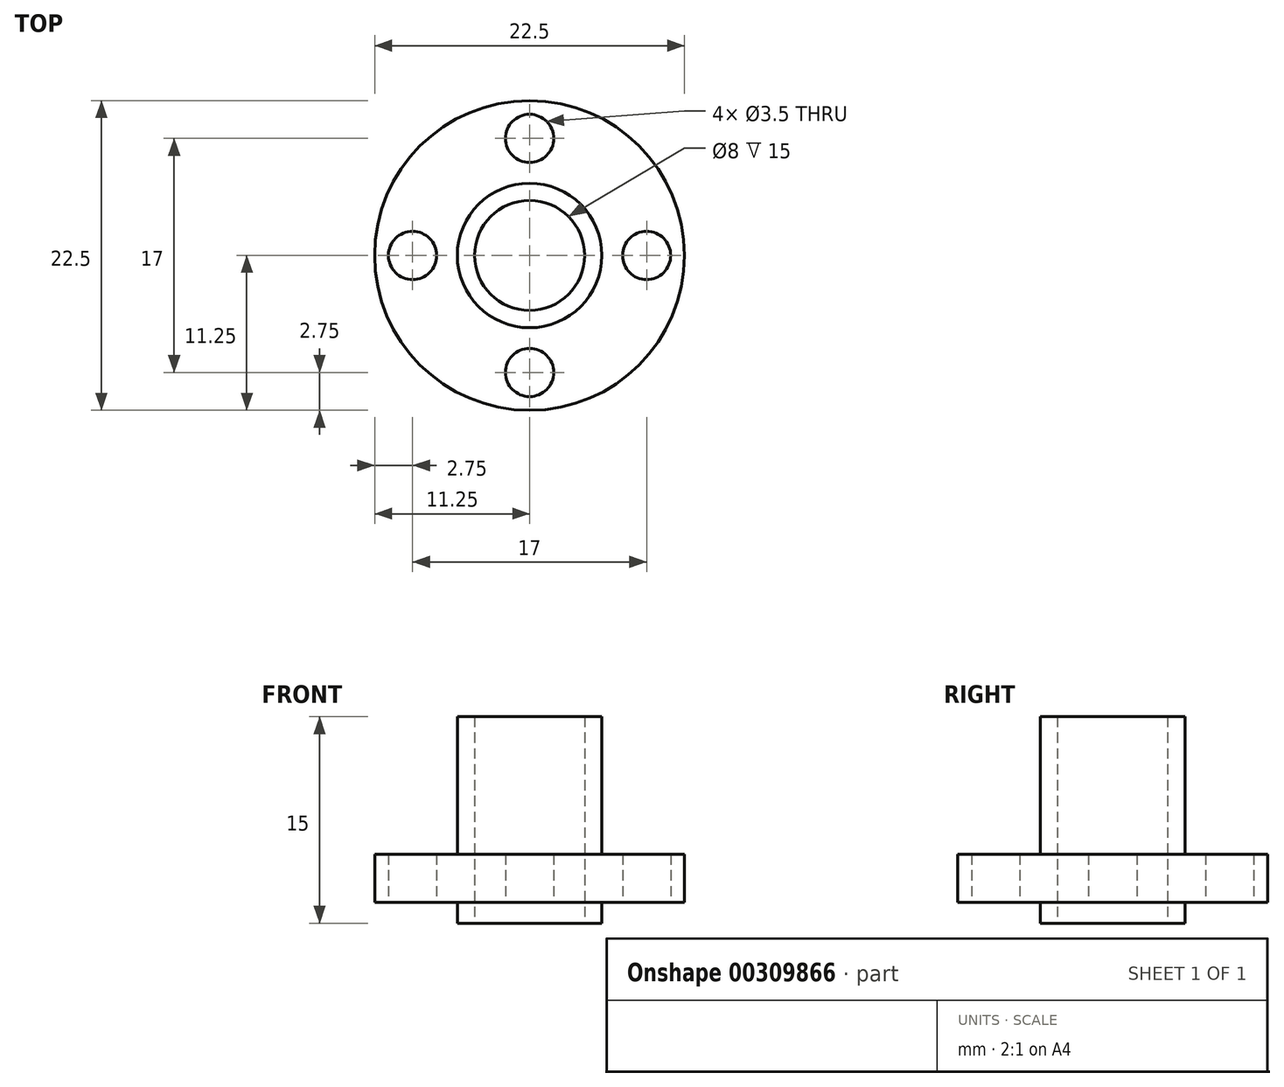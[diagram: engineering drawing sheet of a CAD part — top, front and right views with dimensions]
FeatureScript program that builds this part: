
annotation { "Feature Type Name" : "Feature", "Feature Type Description" : "" }
export const myFeature = defineFeature(function(context is Context, id is Id, definition is map)
    precondition{}
    {
        {
            var Q0;
            Q0=qCreatedBy(makeId("Front.planeOp"),FACE);
            var sketch = newSketch(context, id + "F0", { "sketchPlane" : qUnion([Q0])});
            skLineSegment(sketch, "E0", {"start": v(11.25, 3.5) * mm, "end": v(11.25, 0) * mm});
            skLineSegment(sketch, "E1", {"start": v(11.25, 0) * mm, "end": v(5.25, 0) * mm});
            skLineSegment(sketch, "E2", {"start": v(5.25, 3.5) * mm, "end": v(11.25, 3.5) * mm});
            skLineSegment(sketch, "E3", {"start": v(5.25, 3.5) * mm, "end": v(5.25, 13.5) * mm});
            skLineSegment(sketch, "E4", {"start": v(5.25, 0) * mm, "end": v(5.25, -1.5) * mm});
            skLineSegment(sketch, "E5", {"start": v(5.25, -1.5) * mm, "end": v(0, -1.5) * mm});
            skPoint(sketch, "E6.end.orphan", {"position": v(0, 13.5) * mm});
            skLineSegment(sketch, "E7", {"start": v(0, -1.5) * mm, "end": v(0, 13.5) * mm});
            skLineSegment(sketch, "E8", {"start": v(5.25, 13.5) * mm, "end": v(0, 13.5) * mm});
            skSolve(sketch);
        }
        {
            var Q0;
            Q0=makeQuery(id+"F0.imprint","IMPRINT",FACE,{"disambiguationData":[TD([[makeQuery(id+"F0.imprint","IMPRINT",EDGE,{"derivedFrom":sQuery(id+"F0.wireOp",EDGE,"E0")}),-1.0]])]});
            var Q1;
            Q1=sQuery(id+"F0.wireOp",EDGE,"E7");
            revolve(context, id + "F1", {"entities" : qUnion([Q0]), "axis" : qUnion([Q1]), "revolveType" : RevolveType.FULL});
        }
        {
            var Q0;
            Q0=makeQuery(id+"F1.opRevolve","SWEPT_FACE",FACE,{"disambiguationData":[OSD([sQuery(id+"F0.wireOp",EDGE,"E5")])]});
            var sketch = newSketch(context, id + "F2", { "sketchPlane" : qUnion([Q0])});
            skPoint(sketch, "E9", {"position": v(0, 0) * mm});
            skSolve(sketch);
        }
        {
            var Q0;
            Q0=sQuery(id+"F2.wireOp",VERTEX,"E9");
            var Q1;
            Q1=makeQuery(id+"F1.opRevolve","SWEPT_BODY",BODY,{"disambiguationData":[OSD([sQuery(id+"F0.wireOp",EDGE,"E0"),sQuery(id+"F0.wireOp",EDGE,"E1"),sQuery(id+"F0.wireOp",EDGE,"E2"),sQuery(id+"F0.wireOp",EDGE,"E3"),sQuery(id+"F0.wireOp",EDGE,"E4"),sQuery(id+"F0.wireOp",EDGE,"E5"),sQuery(id+"F0.wireOp",EDGE,"E7"),sQuery(id+"F0.wireOp",EDGE,"E8")])]});
            hole(context, id + "F3", {"style" : HoleStyle.SIMPLE, "endStyle" : HoleEndStyle.THROUGH, "holeDiameter" : (8) * mm, "tappedDepth" : 12 * mm, "tapClearance" : 3, "locations" : qUnion([Q0]), "scope" : qUnion([Q1])});
        }
        {
            var Q0;
            Q0=makeQuery(id+"F1.opRevolve","SWEPT_FACE",FACE,{"disambiguationData":[OSD([sQuery(id+"F0.wireOp",EDGE,"E1")])]});
            var sketch = newSketch(context, id + "F4", { "sketchPlane" : qUnion([Q0])});
            skLineSegment(sketch, "E10", {"start": v(0, 11.25) * mm, "end": v(0, -11.25) * mm, "construction": true});
            skPoint(sketch, "E11", {"position": v(0, 8.5) * mm});
            skPoint(sketch, "E12.center", {"position": v(0, 0) * mm});
            skLineSegment(sketch, "E12.anchor1", {"start": v(0, 0) * mm, "end": v(0, 8.5) * mm, "construction": true});
            skLineSegment(sketch, "E12.anchor2", {"start": v(0, 0) * mm, "end": v(-8.5, 0) * mm, "construction": true});
            skPoint(sketch, "E13.1.0", {"position": v(8.5, 0) * mm});
            skPoint(sketch, "E13.2.0", {"position": v(0, -8.5) * mm});
            skPoint(sketch, "E13.3.0", {"position": v(-8.5, 0) * mm});
            skSolve(sketch);
        }
        {
            var Q0;
            Q0=sQuery(id+"F4.wireOp",VERTEX,"E11");
            var Q1;
            Q1=sQuery(id+"F4.wireOp",VERTEX,"E13.1.0");
            var Q2;
            Q2=sQuery(id+"F4.wireOp",VERTEX,"E13.2.0");
            var Q3;
            Q3=sQuery(id+"F4.wireOp",VERTEX,"E13.3.0");
            var Q4;
            Q4=makeQuery(id+"F1.opRevolve","SWEPT_BODY",BODY,{"disambiguationData":[OSD([sQuery(id+"F0.wireOp",EDGE,"E0"),sQuery(id+"F0.wireOp",EDGE,"E1"),sQuery(id+"F0.wireOp",EDGE,"E2"),sQuery(id+"F0.wireOp",EDGE,"E3"),sQuery(id+"F0.wireOp",EDGE,"E4"),sQuery(id+"F0.wireOp",EDGE,"E5"),sQuery(id+"F0.wireOp",EDGE,"E7"),sQuery(id+"F0.wireOp",EDGE,"E8")])]});
            hole(context, id + "F5", {"style" : HoleStyle.SIMPLE, "endStyle" : HoleEndStyle.THROUGH, "holeDiameter" : 3.5 * mm, "tappedDepth" : 12 * mm, "tapClearance" : 3, "locations" : qUnion([Q0, Q1, Q2, Q3]), "scope" : qUnion([Q4])});
        }
    });
